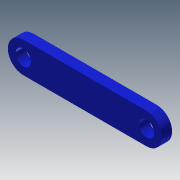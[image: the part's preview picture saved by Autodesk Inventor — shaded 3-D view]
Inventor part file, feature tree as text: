
AUTODESK INVENTOR PART (.ipt)
format: ipt  version: 2015 (Build 190159000, 159)  size: 96,768 bytes
history: native  units: mm
features: extrude x2, sketch x2
ambient origin geometry x8: Origin, YZ Plane, XZ Plane, XY Plane, X Axis, Y Axis, Z Axis, Center Point
bodies: Solid1 (feature_tree)
feature tree (4):
  extrude  "Extrusion1"  Depth=6.0mm
  extrude  "Extrusion2"  Depth=6.0mm
  sketch  "Sketch1"  dims[d0=24.0mm d1=6.0mm]
  sketch  "Sketch2"  dims[d2=6.0mm d3=6.0mm d4=2.0mm d5=0.0mm d6=2.0mm d7=3.0mm d8=3.0mm d9=2.0mm d10=0.0mm]
